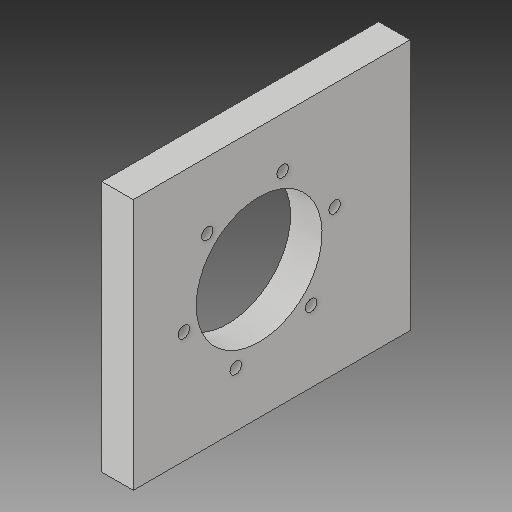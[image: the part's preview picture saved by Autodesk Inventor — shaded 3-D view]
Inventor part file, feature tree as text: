
AUTODESK INVENTOR PART (.ipt)
format: ipt  version: 2019 (Build 230136000, 136)  size: 130,048 bytes
history: native  units: in
note: dims shown in document units (in); Inventor stores cm internally (conversion verified against a paired STEP export)
features: other x3, sketch x3
ambient origin geometry x8: Origin, YZ Plane, XZ Plane, XY Plane, X Axis, Y Axis, Z Axis, Center Point
bodies: Solid1 (feature_tree)
feature tree (6):
  other  "motor mount.ipt"
  other  "Solid1::motor mount.ipt"
  other  "TaggingFeature1"
  sketch  "Sketch1"  dims[d0=0.3937in]
  sketch  "Sketch2"
  sketch  "Sketch3"
